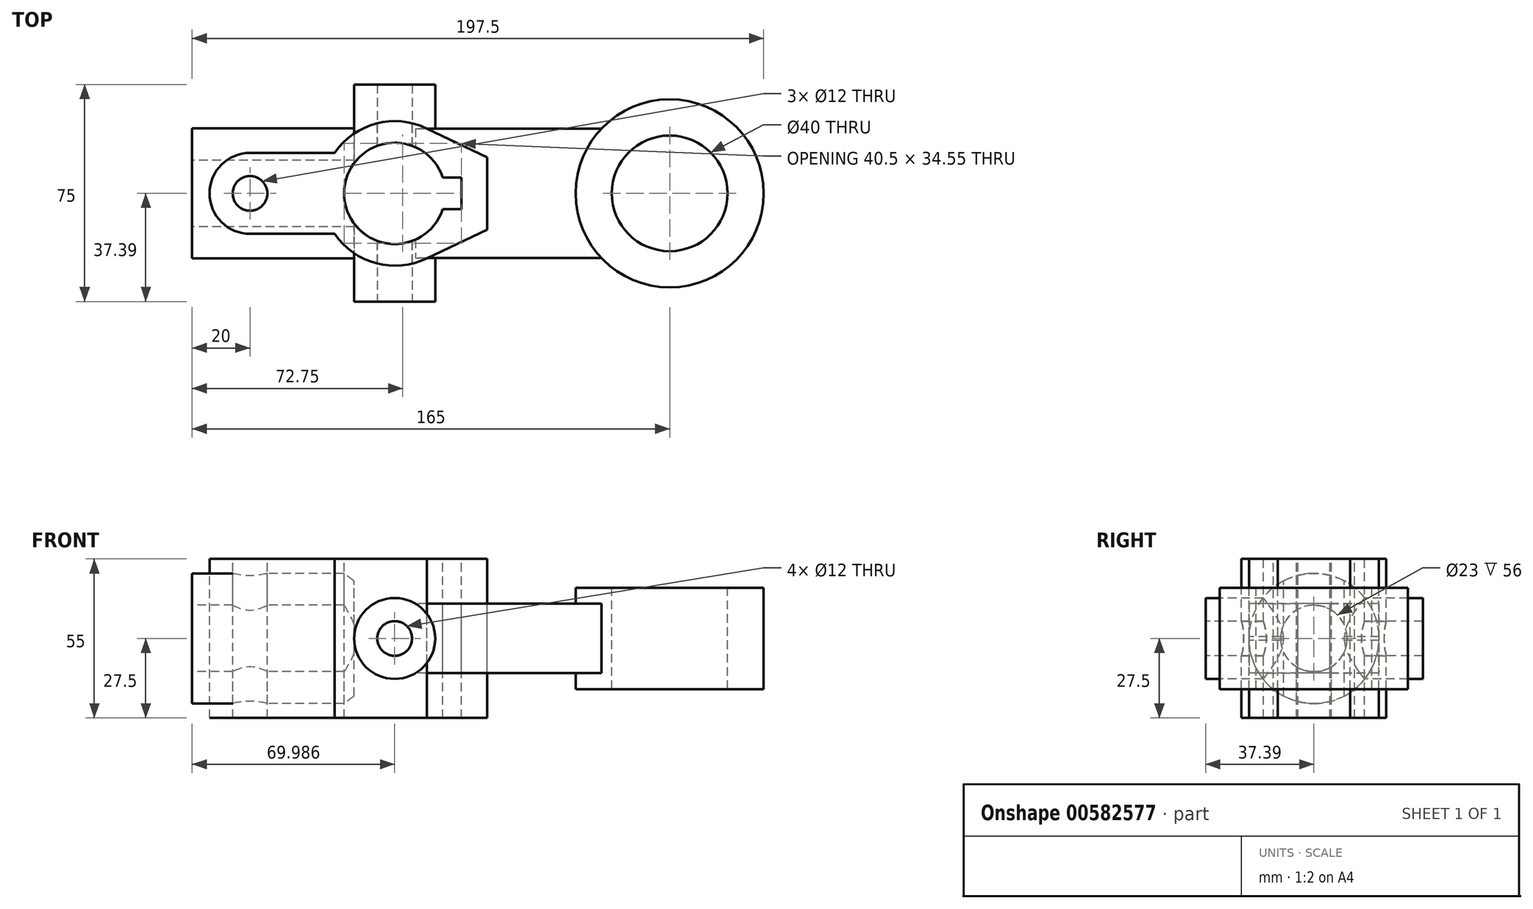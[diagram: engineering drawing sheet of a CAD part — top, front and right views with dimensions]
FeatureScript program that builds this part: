
annotation { "Feature Type Name" : "Feature", "Feature Type Description" : "" }
export const myFeature = defineFeature(function(context is Context, id is Id, definition is map)
    precondition{}
    {
        {
            var Q0;
            Q0=qCreatedBy(makeId("Top.planeOp"),FACE);
            var sketch = newSketch(context, id + "F0", { "sketchPlane" : qUnion([Q0])});
            skCircle(sketch, "E0", {"center": v(0, 0) * mm, "radius": 32.5 * mm});
            skSolve(sketch);
        }
        {
            var Q0;
            Q0=makeQuery(id+"F0.imprint","IMPRINT",FACE,{"disambiguationData":[TD([[makeQuery(id+"F0.imprint","IMPRINT",EDGE,{"derivedFrom":sQuery(id+"F0.wireOp",EDGE,"E0")}),1.0]])]});
            extrude(context, id + "F1", {"entities" : qUnion([Q0]), "depth" : 17.5 * mm, "offsetDistance" : 25 * mm, "hasSecondDirection" : true, "secondDirectionOppositeDirection" : true, "secondDirectionDepth" : 17.5 * mm});
        }
        {
            var Q0;
            Q0=makeQuery(id+"F1.opExtrude","CAP_FACE",FACE,{"disambiguationData":[OSD([sQuery(id+"F0.wireOp",EDGE,"E0")])],"isStart":false});
            var sketch = newSketch(context, id + "F2", { "sketchPlane" : qUnion([Q0])});
            skCircle(sketch, "E1", {"center": v(0, 0) * mm, "radius": 20 * mm});
            skSolve(sketch);
        }
        {
            var Q0;
            Q0=makeQuery(id+"F2.imprint","IMPRINT",FACE,{"disambiguationData":[TD([[makeQuery(id+"F2.imprint","IMPRINT",EDGE,{"derivedFrom":sQuery(id+"F2.wireOp",EDGE,"E1")}),1.0]])]});
            extrude(context, id + "F3", {"entities" : qUnion([Q0]), "operationType" : NewBodyOperationType.REMOVE, "endBound" : BoundingType.THROUGH_ALL, "oppositeDirection" : true, "depth" : 25 * mm, "offsetDistance" : 25 * mm});
        }
        {
            var Q0;
            Q0=qCreatedBy(makeId("Right.planeOp"),FACE);
            cPlane(context, id + "F4", {"entities" : qUnion([Q0]), "cplaneType" : CPlaneType.OFFSET, "offset" : 95 * mm, "oppositeDirection" : true, "width" : 150 * mm, "height" : 150 * mm});
        }
        {
            var Q0;
            Q0=qCreatedBy(id+"F4.planeOp",FACE);
            var sketch = newSketch(context, id + "F5", { "sketchPlane" : qUnion([Q0])});
            skLineSegment(sketch, "E2.bottom", {"start": v(-22.4, 12) * mm, "end": v(22.4, 12) * mm});
            skLineSegment(sketch, "E2.top", {"start": v(-22.4, -12) * mm, "end": v(22.4, -12) * mm});
            skLineSegment(sketch, "E2.left", {"start": v(-22.4, 12) * mm, "end": v(-22.4, -12) * mm});
            skLineSegment(sketch, "E2.right", {"start": v(22.4, 12) * mm, "end": v(22.4, -12) * mm});
            skPoint(sketch, "E2.middle", {"position": v(0, 0) * mm});
            skSolve(sketch);
        }
        {
            var Q0;
            Q0=makeQuery(id+"F5.imprint","IMPRINT",FACE,{"disambiguationData":[TD([[makeQuery(id+"F5.imprint","IMPRINT",EDGE,{"derivedFrom":sQuery(id+"F5.wireOp",EDGE,"E2.bottom")}),-1.0]])]});
            var Q1;
            Q1=makeQuery(id+"F1.opExtrude","SWEPT_FACE",FACE,{"disambiguationData":[OSD([sQuery(id+"F0.wireOp",EDGE,"E0")])]});
            extrude(context, id + "F6", {"entities" : qUnion([Q0]), "operationType" : NewBodyOperationType.ADD, "endBound" : BoundingType.UP_TO_SURFACE, "depth" : 25 * mm, "endBoundEntityFace" : qUnion([Q1]), "offsetDistance" : 25 * mm});
        }
        {
            var Q0;
            Q0=makeQuery(id+"F6.opExtrude","SWEPT_FACE",FACE,{"disambiguationData":[OSD([sQuery(id+"F5.wireOp",EDGE,"E2.left")])]});
            cPlane(context, id + "F7", {"entities" : qUnion([Q0]), "cplaneType" : CPlaneType.OFFSET, "offset" : 15 * mm, "width" : 150 * mm, "height" : 150 * mm});
        }
        {
            var Q0;
            Q0=qCreatedBy(id+"F7.planeOp",FACE);
            var sketch = newSketch(context, id + "F8", { "sketchPlane" : qUnion([Q0])});
            skCircle(sketch, "E3", {"center": v(-95.01, 0) * mm, "radius": 14 * mm});
            skSolve(sketch);
        }
        {
            var Q0;
            Q0=makeQuery(id+"F8.imprint","IMPRINT",FACE,{"disambiguationData":[TD([[makeQuery(id+"F8.imprint","IMPRINT",EDGE,{"derivedFrom":sQuery(id+"F8.wireOp",EDGE,"E3")}),1.0]])]});
            extrude(context, id + "F9", {"entities" : qUnion([Q0]), "operationType" : NewBodyOperationType.ADD, "oppositeDirection" : true, "depth" : 75 * mm, "offsetDistance" : 25 * mm});
        }
        {
            var Q0;
            Q0=makeQuery(id+"F9.opExtrude","CAP_FACE",FACE,{"disambiguationData":[OSD([sQuery(id+"F8.wireOp",EDGE,"E3")])],"isStart":true});
            var sketch = newSketch(context, id + "F10", { "sketchPlane" : qUnion([Q0])});
            skCircle(sketch, "E4", {"center": v(-95.01, 0) * mm, "radius": 6 * mm});
            skSolve(sketch);
        }
        {
            var Q0;
            Q0 = qSketchRegion(id + "F10", true);
            extrude(context, id + "F11", {"entities" : qUnion([Q0]), "operationType" : NewBodyOperationType.REMOVE, "endBound" : BoundingType.THROUGH_ALL, "oppositeDirection" : true, "depth" : 25 * mm, "offsetDistance" : 25 * mm});
        }
        {
            var Q0;
            Q0=qCreatedBy(makeId("Right.planeOp"),FACE);
            cPlane(context, id + "F12", {"entities" : qUnion([Q0]), "cplaneType" : CPlaneType.OFFSET, "offset" : 165 * mm, "oppositeDirection" : true, "width" : 150 * mm, "height" : 150 * mm});
        }
        {
            var Q0;
            Q0=qCreatedBy(id+"F12.planeOp",FACE);
            var sketch = newSketch(context, id + "F13", { "sketchPlane" : qUnion([Q0])});
            skCircle(sketch, "E5", {"center": v(0, 0) * mm, "radius": 22.5 * mm});
            skSolve(sketch);
        }
        {
            var Q0;
            Q0=makeQuery(id+"F13.imprint","IMPRINT",FACE,{"disambiguationData":[TD([[makeQuery(id+"F13.imprint","IMPRINT",EDGE,{"derivedFrom":sQuery(id+"F13.wireOp",EDGE,"E5")}),1.0]])]});
            extrude(context, id + "F14", {"entities" : qUnion([Q0]), "operationType" : NewBodyOperationType.ADD, "depth" : 56 * mm, "offsetDistance" : 25 * mm});
        }
        {
            var Q0;
            Q0=makeQuery(id+"F14.opExtrude","CAP_FACE",FACE,{"disambiguationData":[OSD([sQuery(id+"F13.wireOp",EDGE,"E5")])],"isStart":true});
            var sketch = newSketch(context, id + "F15", { "sketchPlane" : qUnion([Q0])});
            skCircle(sketch, "E6", {"center": v(0, 0) * mm, "radius": 11.5 * mm});
            skSolve(sketch);
        }
        {
            var Q0;
            Q0=makeQuery(id+"F15.imprint","IMPRINT",FACE,{"disambiguationData":[TD([[makeQuery(id+"F15.imprint","IMPRINT",EDGE,{"derivedFrom":sQuery(id+"F15.wireOp",EDGE,"E6")}),1.0]])]});
            extrude(context, id + "F16", {"entities" : qUnion([Q0]), "operationType" : NewBodyOperationType.REMOVE, "oppositeDirection" : true, "depth" : 56 * mm, "offsetDistance" : 25 * mm});
        }
        {
            var Q0;
            Q0=qCreatedBy(makeId("Top.planeOp"),FACE);
            cPlane(context, id + "F17", {"entities" : qUnion([Q0]), "cplaneType" : CPlaneType.OFFSET, "offset" : 27.5 * mm, "width" : 150 * mm, "height" : 150 * mm});
        }
        {
            var Q0;
            Q0=qCreatedBy(id+"F17.planeOp",FACE);
            var sketch = newSketch(context, id + "F18", { "sketchPlane" : qUnion([Q0])});
            skArc(sketch, "E7", {"start": v(-83.91, 22.4) * mm, "mid": v(-101.39, 24.17) * mm, "end": v(-115.71, 14) * mm});
            skLineSegment(sketch, "E8", {"start": v(-95, 0) * mm, "end": v(-63, 0) * mm});
            skLineSegment(sketch, "E9", {"start": v(-63, 0) * mm, "end": v(-63, -12.5) * mm});
            skLineSegment(sketch, "E10", {"start": v(-63, 0) * mm, "end": v(-63, 12.5) * mm});
            skLineSegment(sketch, "E11", {"start": v(-83.91, 22.4) * mm, "end": v(-63, 12.5) * mm});
            skLineSegment(sketch, "E12", {"start": v(-83.92, -22.41) * mm, "end": v(-63, -12.5) * mm});
            skArc(sketch, "E13", {"start": v(-145, 14) * mm, "mid": v(-159, 0) * mm, "end": v(-145, -14) * mm});
            skLineSegment(sketch, "E14", {"start": v(-145, -14) * mm, "end": v(-115.71, -14) * mm});
            skLineSegment(sketch, "E15", {"start": v(-145, 14) * mm, "end": v(-115.71, 14) * mm});
            skArc(sketch, "E16.trimOffspring", {"start": v(-115.71, -14) * mm, "mid": v(-101.4, -24.17) * mm, "end": v(-83.92, -22.41) * mm});
            skSolve(sketch);
        }
        {
            var Q0;
            Q0 = qSketchRegion(id + "F18", true);
            extrude(context, id + "F19", {"entities" : qUnion([Q0]), "oppositeDirection" : true, "depth" : 55 * mm, "offsetDistance" : 25 * mm});
        }
        {
            var Q0;
            Q0=makeQuery(id+"F19.opExtrude","CAP_FACE",FACE,{"disambiguationData":[OSD([sQuery(id+"F18.wireOp",EDGE,"E7"),sQuery(id+"F18.wireOp",EDGE,"E9"),sQuery(id+"F18.wireOp",EDGE,"E10"),sQuery(id+"F18.wireOp",EDGE,"E11"),sQuery(id+"F18.wireOp",EDGE,"E12"),sQuery(id+"F18.wireOp",EDGE,"E13"),sQuery(id+"F18.wireOp",EDGE,"E14"),sQuery(id+"F18.wireOp",EDGE,"E15"),sQuery(id+"F18.wireOp",EDGE,"E16.trimOffspring")])],"isStart":true});
            var sketch = newSketch(context, id + "F20", { "sketchPlane" : qUnion([Q0])});
            skCircle(sketch, "E17", {"center": v(-145, 0) * mm, "radius": 6 * mm});
            skArc(sketch, "E18", {"start": v(-78.39, 5.5) * mm, "mid": v(-112.5, 0) * mm, "end": v(-78.39, -5.5) * mm});
            skLineSegment(sketch, "E19", {"start": v(-72, 0) * mm, "end": v(-72, -5.5) * mm});
            skLineSegment(sketch, "E20", {"start": v(-72, 0) * mm, "end": v(-72, 5.5) * mm});
            skLineSegment(sketch, "E21", {"start": v(-72, -5.5) * mm, "end": v(-78.39, -5.5) * mm});
            skLineSegment(sketch, "E22", {"start": v(-72, 5.5) * mm, "end": v(-78.39, 5.5) * mm});
            skSolve(sketch);
        }
        {
            var Q0;
            Q0=makeQuery(id+"F20.imprint","IMPRINT",FACE,{"disambiguationData":[TD([[makeQuery(id+"F20.imprint","IMPRINT",EDGE,{"derivedFrom":sQuery(id+"F20.wireOp",EDGE,"E17")}),1.0]])]});
            var Q1;
            Q1=makeQuery(id+"F20.imprint","IMPRINT",FACE,{"disambiguationData":[TD([[makeQuery(id+"F20.imprint","IMPRINT",EDGE,{"derivedFrom":sQuery(id+"F20.wireOp",EDGE,"E18")}),1.0]])]});
            extrude(context, id + "F21", {"entities" : qUnion([Q0, Q1]), "operationType" : NewBodyOperationType.REMOVE, "endBound" : BoundingType.THROUGH_ALL, "oppositeDirection" : true, "depth" : 25 * mm, "offsetDistance" : 25 * mm});
        }
        {
            var Q0;
            Q0=makeQuery(id+"F9.opExtrude","CAP_FACE",FACE,{"disambiguationData":[OSD([sQuery(id+"F8.wireOp",EDGE,"E3")])],"isStart":false});
            var sketch = newSketch(context, id + "F22", { "sketchPlane" : qUnion([Q0])});
            skCircle(sketch, "E23", {"center": v(95.01, 0) * mm, "radius": 6 * mm});
            skSolve(sketch);
        }
        {
            var Q0;
            Q0=makeQuery(id+"F22.imprint","IMPRINT",FACE,{"disambiguationData":[TD([[makeQuery(id+"F22.imprint","IMPRINT",EDGE,{"derivedFrom":sQuery(id+"F22.wireOp",EDGE,"E23")}),-1.0]])]});
            extrude(context, id + "F23", {"entities" : qUnion([Q0]), "operationType" : NewBodyOperationType.REMOVE, "endBound" : BoundingType.THROUGH_ALL, "oppositeDirection" : true, "depth" : 25 * mm, "offsetDistance" : 25 * mm});
        }
    });
